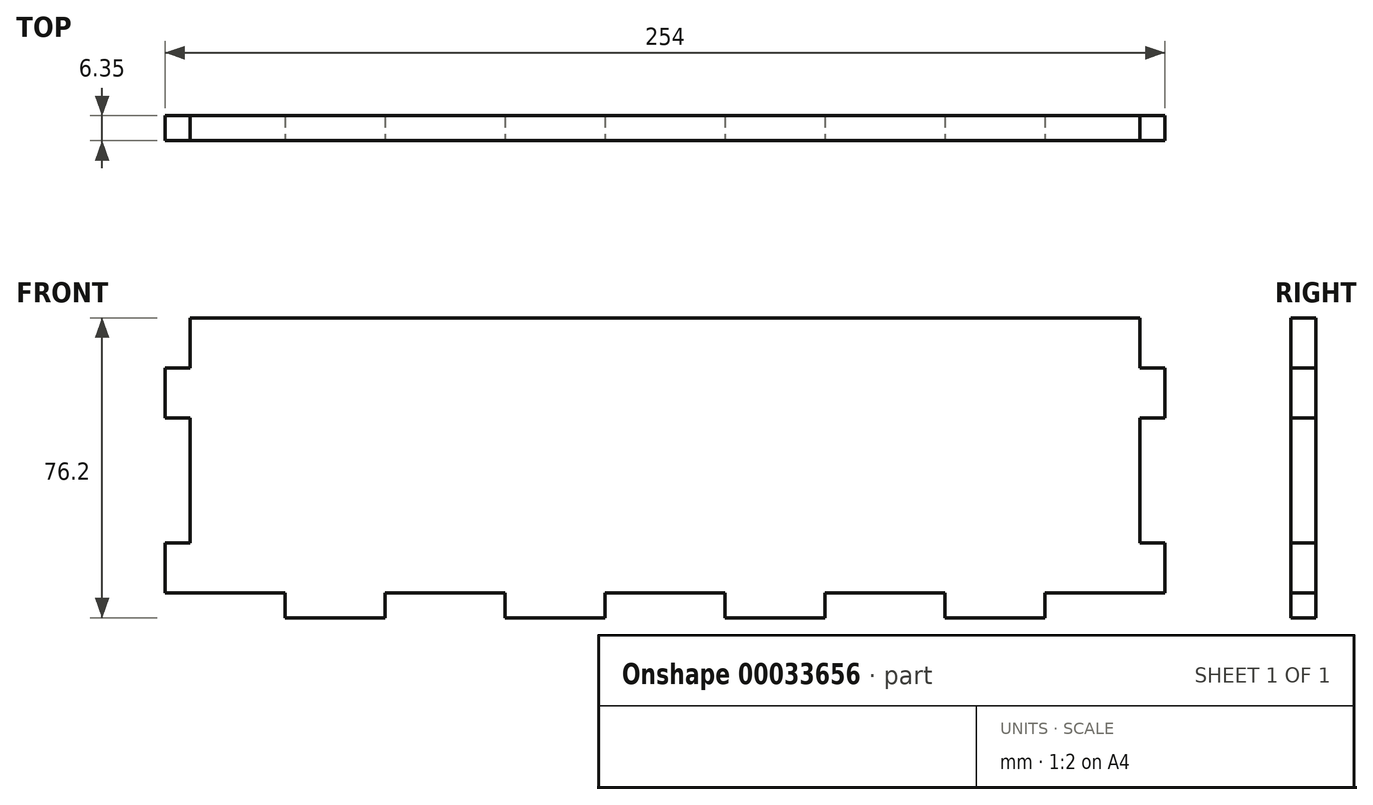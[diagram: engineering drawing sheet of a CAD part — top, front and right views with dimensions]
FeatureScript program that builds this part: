
annotation { "Feature Type Name" : "Feature", "Feature Type Description" : "" }
export const myFeature = defineFeature(function(context is Context, id is Id, definition is map)
    precondition{}
    {
        {
            var Q0;
            Q0=qCreatedBy(makeId("Front.planeOp"),FACE);
            var sketch = newSketch(context, id + "F0", { "sketchPlane" : qUnion([Q0])});
            skLineSegment(sketch, "E0.bottom", {"start": v(0, 0) * mm, "end": v(254, 0) * mm});
            skLineSegment(sketch, "E0.top", {"start": v(0, 76.2) * mm, "end": v(254, 76.2) * mm});
            skLineSegment(sketch, "E0.left", {"start": v(0, 0) * mm, "end": v(0, 76.2) * mm});
            skLineSegment(sketch, "E0.right", {"start": v(254, 0) * mm, "end": v(254, 76.2) * mm});
            skSolve(sketch);
        }
        {
            var Q0;
            Q0=makeQuery(id+"F0.imprint","IMPRINT",FACE,{"disambiguationData":[TD([[makeQuery(id+"F0.imprint","IMPRINT",EDGE,{"derivedFrom":sQuery(id+"F0.wireOp",EDGE,"E0.bottom")}),1.0]])]});
            extrude(context, id + "F1", {"entities" : qUnion([Q0]), "depth" : 6.35 * mm});
        }
        {
            var Q0;
            Q0=makeQuery(id+"F1.opExtrude","CAP_FACE",FACE,{"disambiguationData":[OSD([sQuery(id+"F0.wireOp",EDGE,"E0.bottom"),sQuery(id+"F0.wireOp",EDGE,"E0.top"),sQuery(id+"F0.wireOp",EDGE,"E0.left"),sQuery(id+"F0.wireOp",EDGE,"E0.right")])],"isStart":false});
            var sketch = newSketch(context, id + "F2", { "sketchPlane" : qUnion([Q0])});
            skLineSegment(sketch, "E1", {"start": v(127, 76.2) * mm, "end": v(127, 0) * mm, "construction": true});
            skLineSegment(sketch, "E2.bottom", {"start": v(0, 0) * mm, "end": v(6.35, 0) * mm});
            skLineSegment(sketch, "E2.top", {"start": v(0, 6.35) * mm, "end": v(6.35, 6.35) * mm});
            skLineSegment(sketch, "E2.left", {"start": v(0, 0) * mm, "end": v(0, 6.35) * mm});
            skLineSegment(sketch, "E2.right", {"start": v(6.35, 0) * mm, "end": v(6.35, 6.35) * mm});
            skLineSegment(sketch, "E3.bottom", {"start": v(0, 76.2) * mm, "end": v(6.35, 76.2) * mm});
            skLineSegment(sketch, "E3.top", {"start": v(0, 63.5) * mm, "end": v(6.35, 63.5) * mm});
            skLineSegment(sketch, "E3.left", {"start": v(0, 76.2) * mm, "end": v(0, 63.5) * mm});
            skLineSegment(sketch, "E3.right", {"start": v(6.35, 76.2) * mm, "end": v(6.35, 63.5) * mm});
            skLineSegment(sketch, "E4.bottom", {"start": v(0, 19.05) * mm, "end": v(6.35, 19.05) * mm});
            skLineSegment(sketch, "E4.top", {"start": v(0, 50.8) * mm, "end": v(6.35, 50.8) * mm});
            skLineSegment(sketch, "E4.left", {"start": v(0, 19.05) * mm, "end": v(0, 50.8) * mm});
            skLineSegment(sketch, "E4.right", {"start": v(6.35, 19.05) * mm, "end": v(6.35, 50.8) * mm});
            skLineSegment(sketch, "E5.MirrorCS", {"start": v(254, 6.35) * mm, "end": v(247.65, 6.35) * mm});
            skLineSegment(sketch, "E6.MirrorCS", {"start": v(254, 19.05) * mm, "end": v(247.65, 19.05) * mm});
            skLineSegment(sketch, "E7.MirrorCS", {"start": v(254, 50.8) * mm, "end": v(247.65, 50.8) * mm});
            skLineSegment(sketch, "E8.MirrorCS", {"start": v(254, 0) * mm, "end": v(247.65, 0) * mm});
            skLineSegment(sketch, "E9.MirrorCS", {"start": v(247.65, 76.2) * mm, "end": v(247.65, 63.5) * mm});
            skLineSegment(sketch, "E10.MirrorCS", {"start": v(247.65, 0) * mm, "end": v(247.65, 6.35) * mm});
            skLineSegment(sketch, "E11.MirrorCS", {"start": v(254, 0) * mm, "end": v(254, 6.35) * mm});
            skLineSegment(sketch, "E12.MirrorCS", {"start": v(254, 63.5) * mm, "end": v(247.65, 63.5) * mm});
            skLineSegment(sketch, "E13.MirrorCS", {"start": v(254, 76.2) * mm, "end": v(247.65, 76.2) * mm});
            skLineSegment(sketch, "E14.MirrorCS", {"start": v(254, 76.2) * mm, "end": v(254, 63.5) * mm});
            skLineSegment(sketch, "E15.MirrorCS", {"start": v(247.65, 19.05) * mm, "end": v(247.65, 50.8) * mm});
            skLineSegment(sketch, "E16.MirrorCS", {"start": v(254, 19.05) * mm, "end": v(254, 50.8) * mm});
            skSolve(sketch);
        }
        {
            var Q0;
            Q0=qSketchRegion(id+"F2",true);
            extrude(context, id + "F3", {"entities" : qUnion([Q0]), "operationType" : NewBodyOperationType.REMOVE, "endBound" : BoundingType.UP_TO_NEXT, "oppositeDirection" : true, "depth" : 25.4 * mm});
        }
        {
            var Q0;
            Q0=makeQuery(id+"F1.opExtrude","CAP_FACE",FACE,{"disambiguationData":[OSD([sQuery(id+"F0.wireOp",EDGE,"E0.bottom"),sQuery(id+"F0.wireOp",EDGE,"E0.top"),sQuery(id+"F0.wireOp",EDGE,"E0.left"),sQuery(id+"F0.wireOp",EDGE,"E0.right")])],"isStart":false});
            var sketch = newSketch(context, id + "F4", { "sketchPlane" : qUnion([Q0])});
            skLineSegment(sketch, "E17.bottom", {"start": v(0, 0) * mm, "end": v(30.48, 0) * mm});
            skLineSegment(sketch, "E17.top", {"start": v(0, 6.35) * mm, "end": v(30.48, 6.35) * mm});
            skLineSegment(sketch, "E17.left", {"start": v(0, 0) * mm, "end": v(0, 6.35) * mm});
            skLineSegment(sketch, "E17.right", {"start": v(30.48, 0) * mm, "end": v(30.48, 6.35) * mm});
            skLineSegment(sketch, "E18.1.0.0", {"start": v(86.36, 0) * mm, "end": v(86.36, 6.35) * mm});
            skLineSegment(sketch, "E18.1.0.1", {"start": v(55.88, 0) * mm, "end": v(55.88, 6.35) * mm});
            skLineSegment(sketch, "E18.1.0.2", {"start": v(55.88, 6.35) * mm, "end": v(86.36, 6.35) * mm});
            skLineSegment(sketch, "E18.1.0.3", {"start": v(55.88, 0) * mm, "end": v(86.36, 0) * mm});
            skLineSegment(sketch, "E18.2.0.0", {"start": v(142.24, 0) * mm, "end": v(142.24, 6.35) * mm});
            skLineSegment(sketch, "E18.2.0.1", {"start": v(111.76, 0) * mm, "end": v(111.76, 6.35) * mm});
            skLineSegment(sketch, "E18.2.0.2", {"start": v(111.76, 6.35) * mm, "end": v(142.24, 6.35) * mm});
            skLineSegment(sketch, "E18.2.0.3", {"start": v(111.76, 0) * mm, "end": v(142.24, 0) * mm});
            skLineSegment(sketch, "E18.3.0.0", {"start": v(198.12, 0) * mm, "end": v(198.12, 6.35) * mm});
            skLineSegment(sketch, "E18.3.0.1", {"start": v(167.64, 0) * mm, "end": v(167.64, 6.35) * mm});
            skLineSegment(sketch, "E18.3.0.2", {"start": v(167.64, 6.35) * mm, "end": v(198.12, 6.35) * mm});
            skLineSegment(sketch, "E18.3.0.3", {"start": v(167.64, 0) * mm, "end": v(198.12, 0) * mm});
            skLineSegment(sketch, "E18.4.0.0", {"start": v(254, 0) * mm, "end": v(254, 6.35) * mm});
            skLineSegment(sketch, "E18.4.0.1", {"start": v(223.52, 0) * mm, "end": v(223.52, 6.35) * mm});
            skLineSegment(sketch, "E18.4.0.2", {"start": v(223.52, 6.35) * mm, "end": v(254, 6.35) * mm});
            skLineSegment(sketch, "E18.4.0.3", {"start": v(223.52, 0) * mm, "end": v(254, 0) * mm});
            skLineSegment(sketch, "E18.direction1", {"start": v(30.48, 0) * mm, "end": v(86.36, 0) * mm, "construction": true});
            skSolve(sketch);
        }
        {
            var Q0;
            Q0=qSketchRegion(id+"F4",true);
            extrude(context, id + "F5", {"entities" : qUnion([Q0]), "operationType" : NewBodyOperationType.REMOVE, "endBound" : BoundingType.THROUGH_ALL, "oppositeDirection" : true, "depth" : 25.4 * mm});
        }
    });
